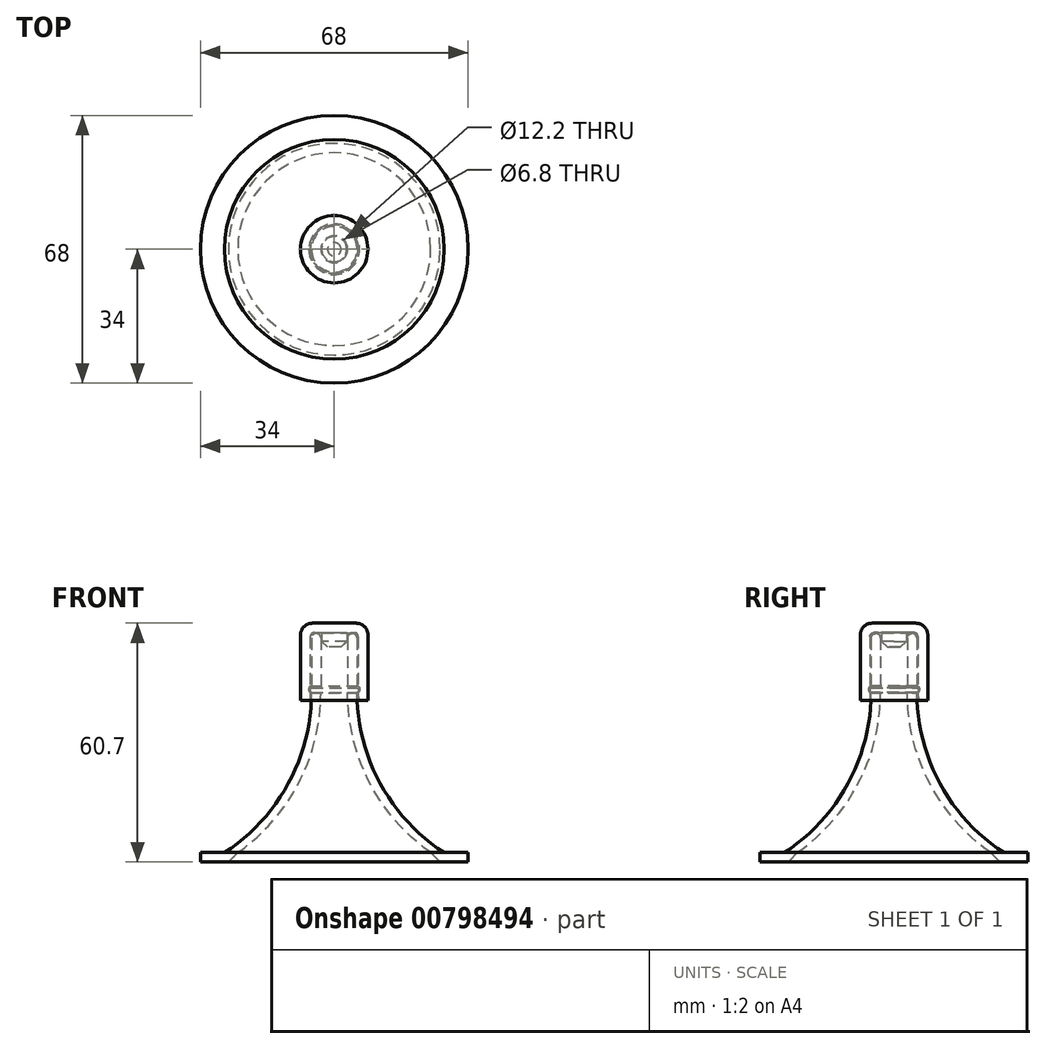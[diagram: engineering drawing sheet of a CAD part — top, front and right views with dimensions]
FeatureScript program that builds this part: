
annotation { "Feature Type Name" : "Feature", "Feature Type Description" : "" }
export const myFeature = defineFeature(function(context is Context, id is Id, definition is map)
    precondition{}
    {
        {
            var Q0;
            Q0=qCreatedBy(makeId("Front.planeOp"),FACE);
            var sketch = newSketch(context, id + "F0", { "sketchPlane" : qUnion([Q0])});
            skLineSegment(sketch, "E0", {"start": v(0, 0) * mm, "end": v(0, 43) * mm, "construction": true});
            skLineSegment(sketch, "E1", {"start": v(24.5, 0) * mm, "end": v(34, 0) * mm});
            skLineSegment(sketch, "E2", {"start": v(34, 0) * mm, "end": v(34, 2.4) * mm});
            skLineSegment(sketch, "E3", {"start": v(24.5, 0) * mm, "end": v(24.5, 2.4) * mm});
            skArc(sketch, "E4", {"start": v(3.4, 43.1) * mm, "mid": v(8.99, 20.17) * mm, "end": v(24.5, 2.4) * mm});
            skLineSegment(sketch, "E5", {"start": v(3.4, 43.1) * mm, "end": v(3.4, 58.1) * mm});
            skLineSegment(sketch, "E6", {"start": v(3.4, 58.1) * mm, "end": v(5.8, 58.1) * mm});
            skLineSegment(sketch, "E7", {"start": v(5.8, 58.1) * mm, "end": v(5.8, 43.1) * mm});
            skLineSegment(sketch, "E8", {"start": v(34, 2.4) * mm, "end": v(27.9, 2.4) * mm});
            skArc(sketch, "E9", {"start": v(5.8, 43.1) * mm, "mid": v(11.68, 19.94) * mm, "end": v(27.9, 2.4) * mm});
            skArc(sketch, "E10", {"start": v(5.8, 43.1) * mm, "mid": v(6.17, 43.68) * mm, "end": v(5.8, 44.27) * mm});
            skSolve(sketch);
        }
        {
            var Q0;
            Q0=makeQuery(id+"F0.imprint","IMPRINT",FACE,{"disambiguationData":[TD([[makeQuery(id+"F0.imprint","IMPRINT",EDGE,{"derivedFrom":sQuery(id+"F0.wireOp",EDGE,"E1")}),1.0]])]});
            var Q1;
            {var subQ0=sQuery(id+"F0.wireOp",EDGE,"E10");Q1=makeQuery(id+"F0.imprint","IMPRINT",FACE,{"disambiguationData":[TD([[makeQuery(id+"F0.imprint","IMPRINT",EDGE,{"derivedFrom":subQ0}),1.0]])]});}
            var Q2;
            {var subQ0=sQuery(id+"F0.wireOp",EDGE,"au1qeKAb-LKQW-OOx2-l866-QHbtjJBJbq2u");Q2=makeQuery(id+"F0.imprint","IMPRINT",FACE,{"disambiguationData":[TD([[makeQuery(id+"F0.imprint","IMPRINT",EDGE,{"derivedFrom":subQ0}),1.0]])]});}
            var Q3;
            Q3=sQuery(id+"F0.wireOp",EDGE,"E0");
            revolve(context, id + "F1", {"surfaceOperationType" : NewSurfaceOperationType.NEW, "entities" : qUnion([Q0, Q1, Q2]), "axis" : qUnion([Q3]), "revolveType" : RevolveType.FULL});
        }
        {
            var Q0;
            Q0=makeQuery(id+"F1.opRevolve","SWEPT_FACE",FACE,{"disambiguationData":[OSD([sQuery(id+"F0.wireOp",EDGE,"E6")])]});
            fillet(context, id + "F2", {"entities" : qUnion([Q0]), "radius" : 1.2 * mm, "tangentPropagation" : true, "allowEdgeOverflow" : false});
        }
        {
            var Q0;
            Q0=qCreatedBy(makeId("Front.planeOp"),FACE);
            var sketch = newSketch(context, id + "F3", { "sketchPlane" : qUnion([Q0])});
            skLineSegment(sketch, "E11", {"start": v(6.1, 58.3) * mm, "end": v(6.1, 43.03) * mm});
            skLineSegment(sketch, "E12", {"start": v(6.1, 43.03) * mm, "end": v(6.16, 41.1) * mm});
            skLineSegment(sketch, "E13", {"start": v(6.16, 41.1) * mm, "end": v(8.56, 41.1) * mm});
            skLineSegment(sketch, "E14", {"start": v(8.56, 41.1) * mm, "end": v(8.56, 60.7) * mm});
            skLineSegment(sketch, "E15", {"start": v(8.56, 60.7) * mm, "end": v(0, 60.7) * mm});
            skArc(sketch, "E16", {"start": v(6.1, 43.03) * mm, "mid": v(6.48, 43.87) * mm, "end": v(6.1, 44.71) * mm});
            skLineSegment(sketch, "E17", {"start": v(3.2, 58.3) * mm, "end": v(6.1, 58.3) * mm});
            skLineSegment(sketch, "E18", {"start": v(0, 60.7) * mm, "end": v(0, 54.6) * mm});
            skLineSegment(sketch, "E19", {"start": v(3.2, 54.6) * mm, "end": v(0, 54.6) * mm});
            skLineSegment(sketch, "E20", {"start": v(3.2, 54.6) * mm, "end": v(3.2, 58.3) * mm});
            skSolve(sketch);
        }
        {
            var Q0;
            Q0=makeQuery(id+"F3.imprint","IMPRINT",FACE,{"disambiguationData":[TD([[makeQuery(id+"F3.imprint","IMPRINT",EDGE,{"derivedFrom":sQuery(id+"F3.wireOp",EDGE,"E12")}),1.0]])]});
            var Q1;
            Q1=sQuery(id+"F0.wireOp",EDGE,"E0");
            revolve(context, id + "F4", {"surfaceOperationType" : NewSurfaceOperationType.NEW, "entities" : qUnion([Q0]), "axis" : qUnion([Q1]), "revolveType" : RevolveType.FULL});
        }
        {
            var Q0;
            Q0=makeQuery(id+"F4.opRevolve","SWEPT_EDGE",EDGE,{"disambiguationData":[OSD([sQuery(id+"F3.wireOp",EDGE,"E14"),sQuery(id+"F3.wireOp",EDGE,"E15")])]});
            fillet(context, id + "F5", {"entities" : qUnion([Q0]), "radius" : 3 * mm, "tangentPropagation" : true, "allowEdgeOverflow" : false});
        }
        {
            var Q0;
            Q0=makeQuery(id+"F4.opRevolve","SWEPT_EDGE",EDGE,{"disambiguationData":[OSD([sQuery(id+"F3.wireOp",EDGE,"JtuNjlPP-pfZr-8iql-ygRt-3SmrPNyvVoVH"),sQuery(id+"F3.wireOp",EDGE,"FNm1WJhu-lWn7-9wmT-rPLo-CO5a3BP3IO64")])]});
            var Q1;
            Q1=makeQuery(id+"F4.opRevolve","SWEPT_EDGE",EDGE,{"disambiguationData":[OSD([sQuery(id+"F3.wireOp",EDGE,"E19"),sQuery(id+"F3.wireOp",EDGE,"E20")])]});
            chamfer(context, id + "F6", {"entities" : qUnion([Q0, Q1]), "width" : 1.5 * mm, "tangentPropagation" : true});
        }
        {
            var Q0;
            Q0=makeQuery(id+"F1.opRevolve","SWEPT_EDGE",EDGE,{"disambiguationData":[OSD([sQuery(id+"F0.wireOp",EDGE,"E1"),sQuery(id+"F0.wireOp",EDGE,"E3")])]});
            chamfer(context, id + "F7", {"entities" : qUnion([Q0]), "width" : 2.4 * mm, "tangentPropagation" : true});
        }
        {
            var Q0;
            Q0=makeQuery(id+"F4.opRevolve","SWEPT_EDGE",EDGE,{"disambiguationData":[OSD([sQuery(id+"F3.wireOp",EDGE,"E11"),sQuery(id+"F3.wireOp",EDGE,"E17")])]});
            fillet(context, id + "F8", {"entities" : qUnion([Q0]), "radius" : 1 * mm, "tangentPropagation" : true, "allowEdgeOverflow" : false});
        }
    });
